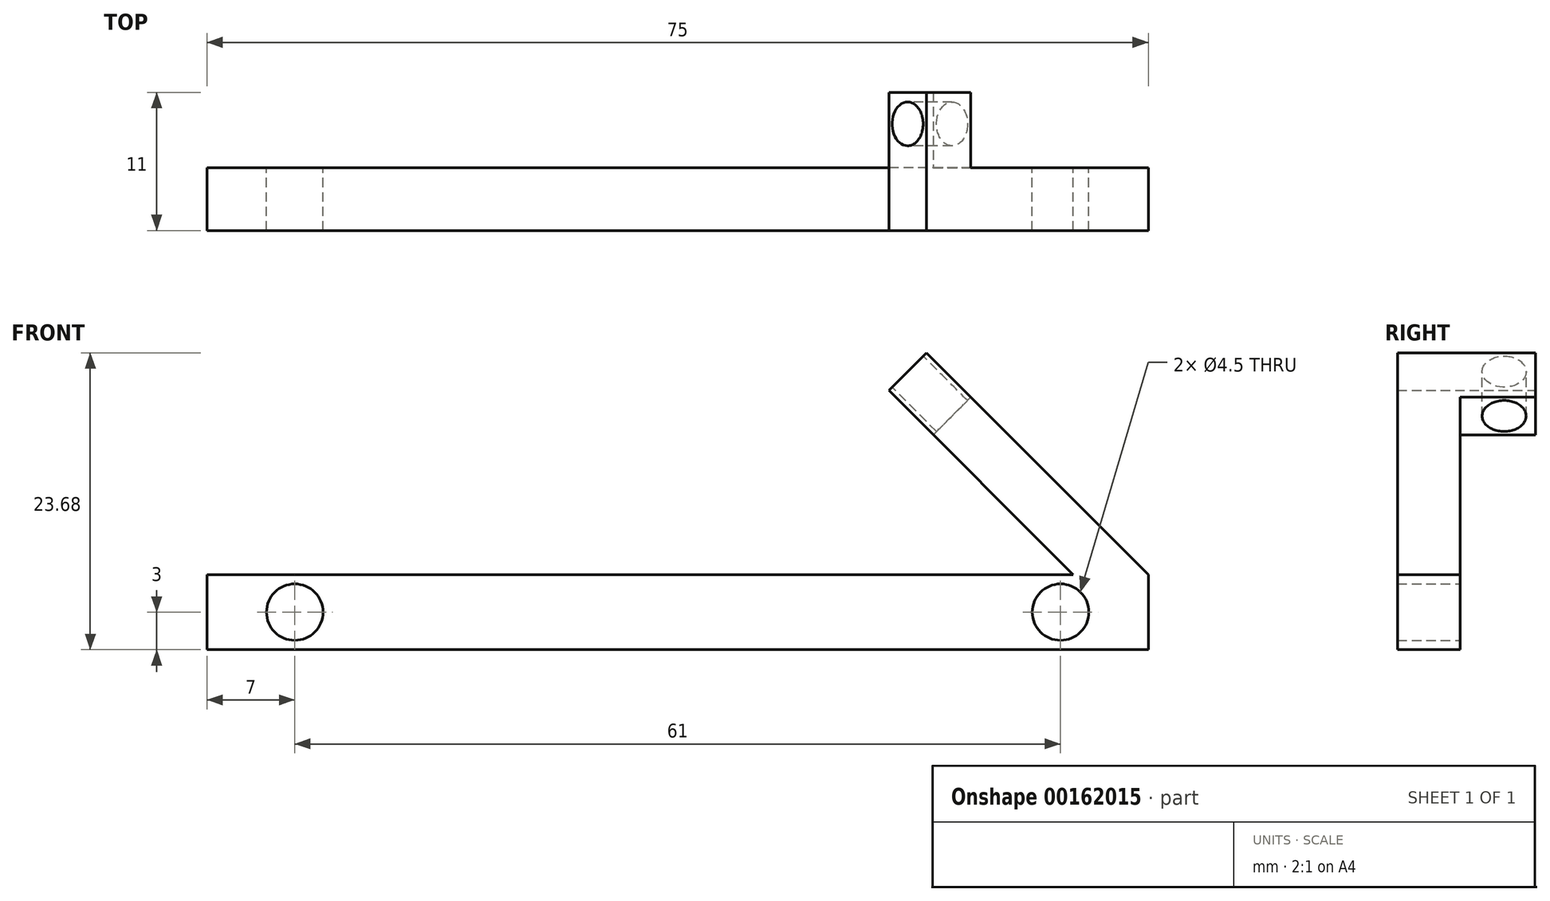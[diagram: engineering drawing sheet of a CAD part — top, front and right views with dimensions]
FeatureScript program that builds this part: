
annotation { "Feature Type Name" : "Feature", "Feature Type Description" : "" }
export const myFeature = defineFeature(function(context is Context, id is Id, definition is map)
    precondition{}
    {
        {
            var Q0;
            Q0=qCreatedBy(makeId("Front.planeOp"),FACE);
            var sketch = newSketch(context, id + "F0", { "sketchPlane" : qUnion([Q0])});
            skLineSegment(sketch, "E0.bottom", {"start": v(37.5, 3) * mm, "end": v(-37.5, 3) * mm});
            skLineSegment(sketch, "E0.top", {"start": v(37.5, -3) * mm, "end": v(-37.5, -3) * mm});
            skLineSegment(sketch, "E0.left", {"start": v(37.5, 3) * mm, "end": v(37.5, -3) * mm});
            skLineSegment(sketch, "E0.right", {"start": v(-37.5, 3) * mm, "end": v(-37.5, -3) * mm});
            skPoint(sketch, "E0.middle", {"position": v(0, 0) * mm});
            skCircle(sketch, "E1", {"center": v(-30.5, 0) * mm, "radius": 2.25 * mm});
            skPoint(sketch, "E1.centerSnap0", {"position": v(-37.5, 0) * mm});
            skLineSegment(sketch, "E2", {"start": v(0, 0) * mm, "end": v(0, 3) * mm, "construction": true});
            skCircle(sketch, "E3.MirrorC", {"center": v(30.5, 0) * mm, "radius": 2.25 * mm});
            skLineSegment(sketch, "E4", {"start": v(37.5, 3) * mm, "end": v(19.82, 20.68) * mm});
            skLineSegment(sketch, "E5", {"start": v(37.5, -3) * mm, "end": v(16.82, 17.68) * mm});
            skLineSegment(sketch, "E6", {"start": v(16.82, 17.68) * mm, "end": v(19.82, 20.68) * mm});
            skSolve(sketch);
        }
        {
            var Q0;
            Q0 = qSketchRegion(id + "F0", true);
            extrude(context, id + "F1", {"entities" : qUnion([Q0]), "depth" : 5 * mm});
        }
        {
            var Q0;
            Q0=makeQuery(id+"F1.opExtrude","CAP_FACE",FACE,{"disambiguationData":[OSD([sQuery(id+"F0.wireOp",EDGE,"E0.bottom"),sQuery(id+"F0.wireOp",EDGE,"E0.top"),sQuery(id+"F0.wireOp",EDGE,"E0.left"),sQuery(id+"F0.wireOp",EDGE,"E0.right"),sQuery(id+"F0.wireOp",EDGE,"E1"),sQuery(id+"F0.wireOp",EDGE,"E3.MirrorC"),sQuery(id+"F0.wireOp",EDGE,"E4"),sQuery(id+"F0.wireOp",EDGE,"E5"),sQuery(id+"F0.wireOp",EDGE,"E6")])],"isStart":true});
            var sketch = newSketch(context, id + "F2", { "sketchPlane" : qUnion([Q0])});
            skLineSegment(sketch, "E7", {"start": v(-16.82, 17.68) * mm, "end": v(-20.36, 14.14) * mm});
            skLineSegment(sketch, "E8", {"start": v(-20.36, 14.14) * mm, "end": v(-23.36, 17.14) * mm});
            skLineSegment(sketch, "E9", {"start": v(-23.36, 17.14) * mm, "end": v(-19.82, 20.68) * mm});
            skLineSegment(sketch, "E10", {"start": v(-19.82, 20.68) * mm, "end": v(-16.82, 17.68) * mm});
            skSolve(sketch);
        }
        {
            var Q0;
            Q0 = qSketchRegion(id + "F2", true);
            extrude(context, id + "F3", {"entities" : qUnion([Q0]), "operationType" : NewBodyOperationType.ADD, "depth" : 6 * mm});
        }
        {
            var Q0;
            Q0=makeQuery(id+"F3.boolean.opBoolean","MERGE",FACE,{"derivedFrom":[makeQuery(id+"F1.opExtrude","SWEPT_FACE",FACE,{"disambiguationData":[OSD([sQuery(id+"F0.wireOp",EDGE,"E6")])]}),makeQuery(id+"F3.opExtrude","SWEPT_FACE",FACE,{"disambiguationData":[OSD([sQuery(id+"F2.wireOp",EDGE,"E10")])]})]});
            var sketch = newSketch(context, id + "F4", { "sketchPlane" : qUnion([Q0])});
            skCircle(sketch, "E11", {"center": v(-3.5, 26.52) * mm, "radius": 1.75 * mm});
            skPoint(sketch, "E11.centerSnap0", {"position": v(-6, 26.52) * mm});
            skSolve(sketch);
        }
        {
            var Q0;
            Q0 = qSketchRegion(id + "F4", true);
            extrude(context, id + "F5", {"entities" : qUnion([Q0]), "operationType" : NewBodyOperationType.REMOVE, "endBound" : BoundingType.THROUGH_ALL, "oppositeDirection" : true, "depth" : 25 * mm});
        }
    });
